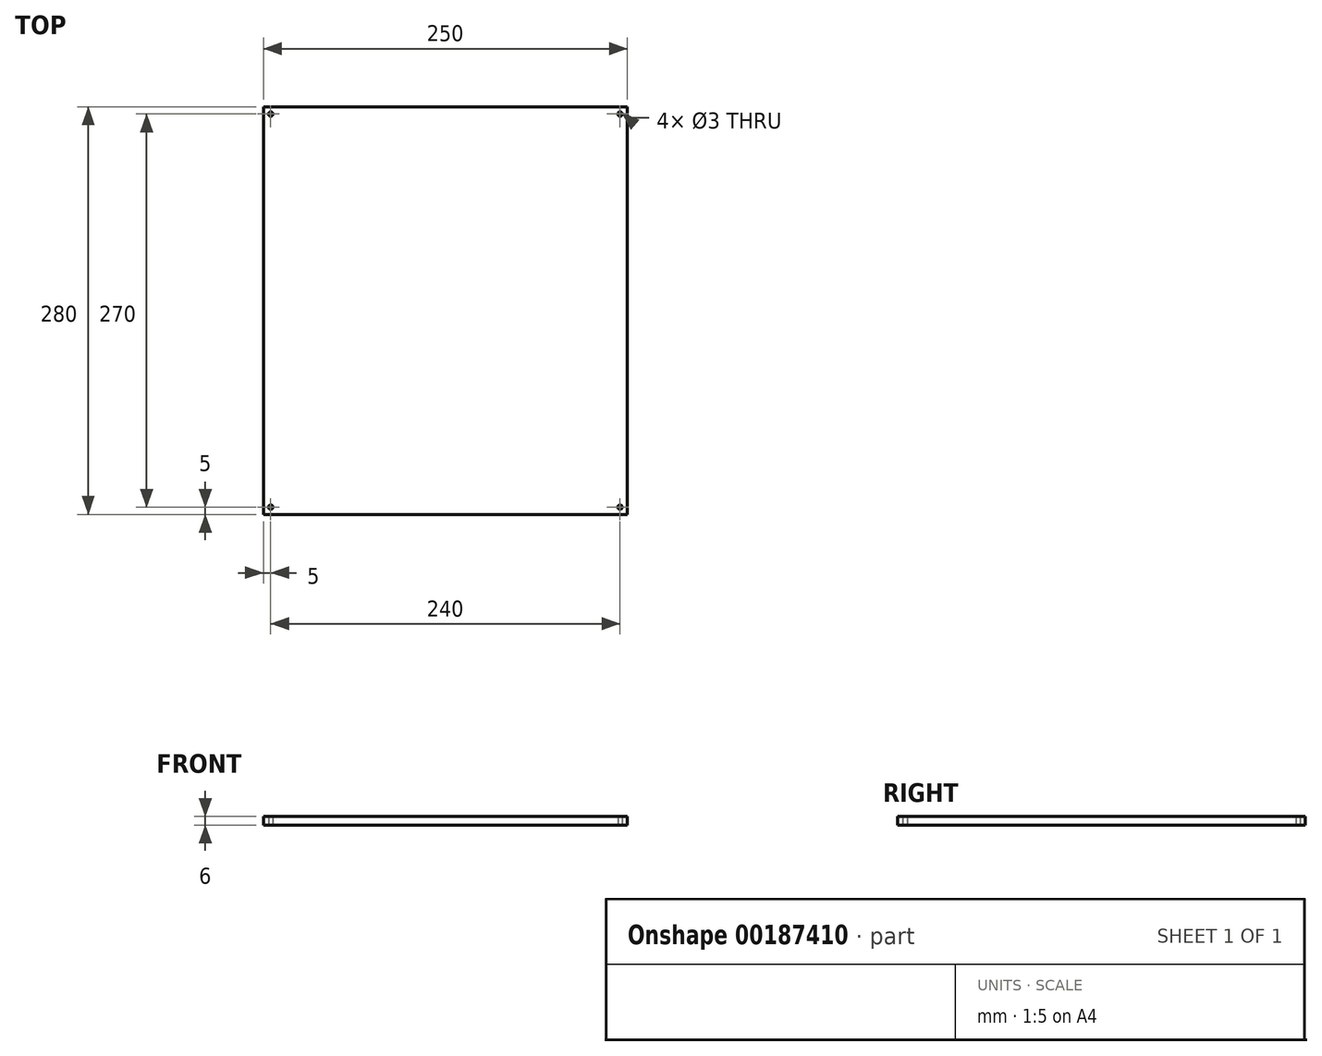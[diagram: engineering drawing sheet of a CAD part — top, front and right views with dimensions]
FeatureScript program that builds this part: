
annotation { "Feature Type Name" : "Feature", "Feature Type Description" : "" }
export const myFeature = defineFeature(function(context is Context, id is Id, definition is map)
    precondition{}
    {
        {
            var Q0;
            Q0=qCreatedBy(makeId("Top.planeOp"),FACE);
            var sketch = newSketch(context, id + "F0", { "sketchPlane" : qUnion([Q0])});
            skLineSegment(sketch, "E0.bottom", {"start": v(-125, -140) * mm, "end": v(125, -140) * mm});
            skLineSegment(sketch, "E0.top", {"start": v(-125, 140) * mm, "end": v(125, 140) * mm});
            skLineSegment(sketch, "E0.left", {"start": v(-125, -140) * mm, "end": v(-125, 140) * mm});
            skLineSegment(sketch, "E0.right", {"start": v(125, -140) * mm, "end": v(125, 140) * mm});
            skPoint(sketch, "E0.middle", {"position": v(0, 0) * mm});
            skCircle(sketch, "E1", {"center": v(-120, 135) * mm, "radius": 1.5 * mm});
            skLineSegment(sketch, "E2", {"start": v(0, 140) * mm, "end": v(0, -140) * mm, "construction": true});
            skLineSegment(sketch, "E3", {"start": v(-125, 0) * mm, "end": v(125, 0) * mm, "construction": true});
            skCircle(sketch, "E4.MirrorC", {"center": v(-120, -135) * mm, "radius": 1.5 * mm});
            skCircle(sketch, "E5.MirrorC", {"center": v(120, -135) * mm, "radius": 1.5 * mm});
            skCircle(sketch, "E6.MirrorC", {"center": v(120, 135) * mm, "radius": 1.5 * mm});
            skSolve(sketch);
        }
        {
            var Q0;
            Q0 = qSketchRegion(id + "F0", true);
            extrude(context, id + "F1", {"entities" : qUnion([Q0]), "depth" : 6 * mm});
        }
    });
